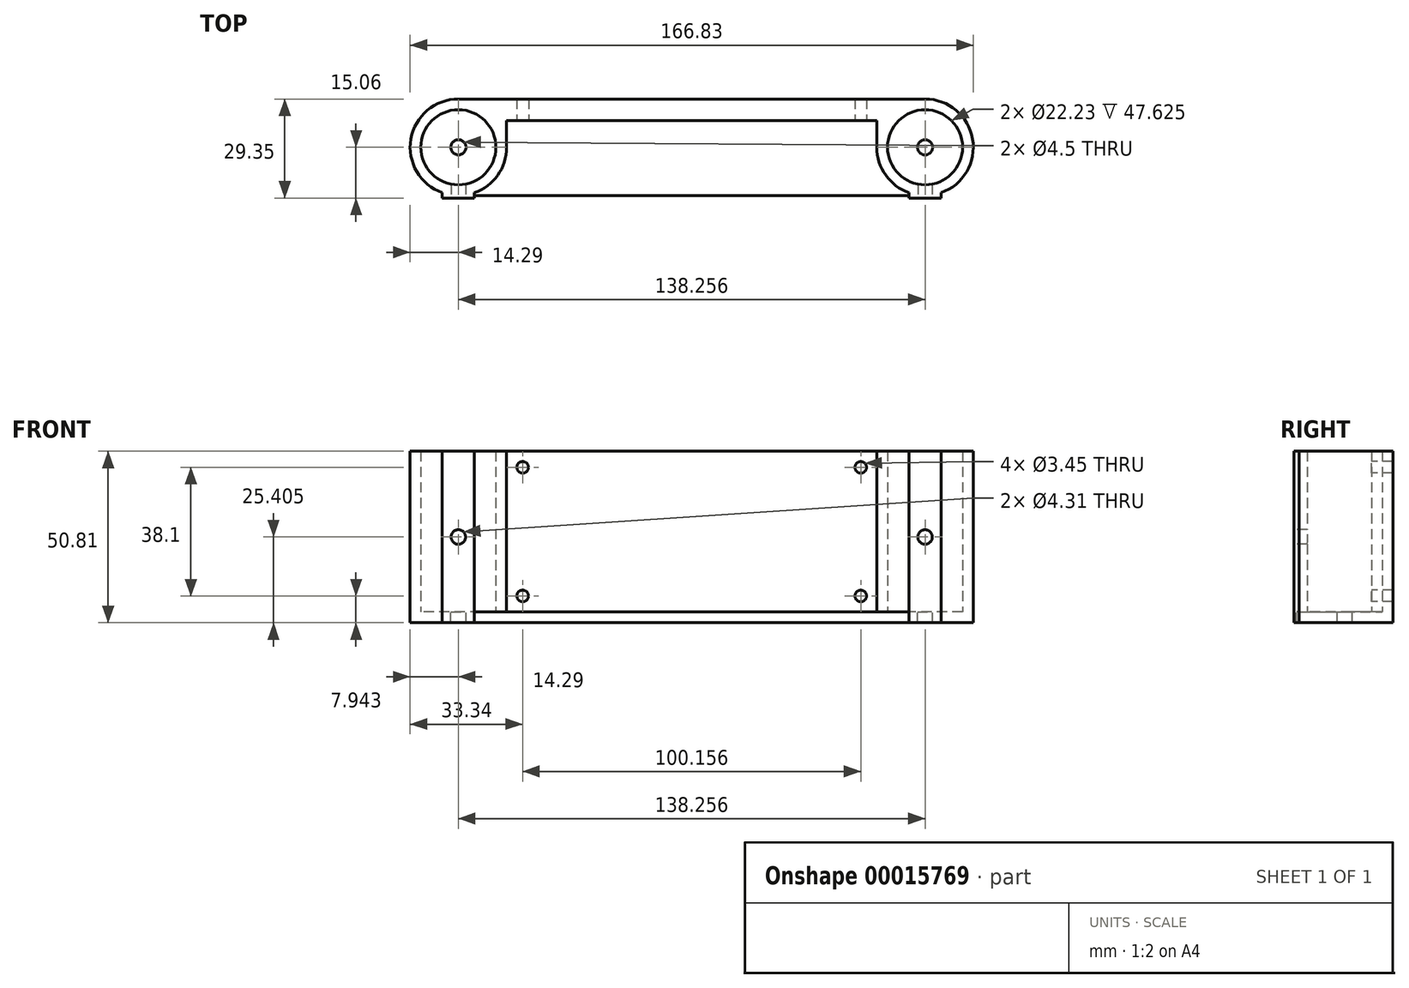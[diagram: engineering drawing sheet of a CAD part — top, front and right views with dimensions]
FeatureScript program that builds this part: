
annotation { "Feature Type Name" : "Feature", "Feature Type Description" : "" }
export const myFeature = defineFeature(function(context is Context, id is Id, definition is map)
    precondition{}
    {
        {
            var Q0;
            Q0=qCreatedBy(makeId("Top.planeOp"),FACE);
            var sketch = newSketch(context, id + "F0", { "sketchPlane" : qUnion([Q0])});
            skCircle(sketch, "E0", {"center": v(0, 0) * mm, "radius": 11.11 * mm});
            skLineSegment(sketch, "E1.bottom", {"start": v(14.29, 7.94) * mm, "end": v(123.97, 7.94) * mm});
            skLineSegment(sketch, "E2", {"start": v(69.13, 7.94) * mm, "end": v(69.13, 14.29) * mm, "construction": true});
            skCircle(sketch, "E3", {"center": v(138.26, 0) * mm, "radius": 11.11 * mm});
            skLineSegment(sketch, "E4", {"start": v(0, 14.29) * mm, "end": v(138.26, 14.29) * mm});
            skLineSegment(sketch, "E5", {"start": v(0, 0) * mm, "end": v(138.26, 0) * mm, "construction": true});
            skLineSegment(sketch, "E6", {"start": v(123.97, 7.94) * mm, "end": v(123.97, 0) * mm});
            skArc(sketch, "E7", {"start": v(0, 14.29) * mm, "mid": v(-14.08, 2.42) * mm, "end": v(-4.76, -13.47) * mm});
            skLineSegment(sketch, "E8", {"start": v(0, 0) * mm, "end": v(0, -13.47) * mm, "construction": true});
            skLineSegment(sketch, "E9", {"start": v(138.26, 0) * mm, "end": v(138.26, -13.47) * mm, "construction": true});
            skLineSegment(sketch, "E10.bottom", {"start": v(-4.76, -13.47) * mm, "end": v(4.76, -13.47) * mm, "construction": true});
            skLineSegment(sketch, "E10.top", {"start": v(-4.76, -15.06) * mm, "end": v(4.76, -15.06) * mm});
            skLineSegment(sketch, "E10.left", {"start": v(-4.76, -13.47) * mm, "end": v(-4.76, -15.06) * mm});
            skLineSegment(sketch, "E10.right", {"start": v(4.76, -13.47) * mm, "end": v(4.76, -15.06) * mm});
            skLineSegment(sketch, "E11.bottom", {"start": v(133.5, -13.47) * mm, "end": v(143.02, -13.47) * mm, "construction": true});
            skLineSegment(sketch, "E11.top", {"start": v(133.5, -15.06) * mm, "end": v(143.02, -15.06) * mm});
            skLineSegment(sketch, "E11.left", {"start": v(133.5, -13.47) * mm, "end": v(133.5, -15.06) * mm});
            skLineSegment(sketch, "E11.right", {"start": v(143.02, -13.47) * mm, "end": v(143.02, -15.06) * mm});
            skArc(sketch, "E12", {"start": v(123.97, 0) * mm, "mid": v(126.6, -8.25) * mm, "end": v(133.5, -13.47) * mm});
            skArc(sketch, "E13", {"start": v(143.02, -13.47) * mm, "mid": v(152.34, 2.42) * mm, "end": v(138.26, 14.29) * mm});
            skLineSegment(sketch, "E14", {"start": v(14.29, 7.94) * mm, "end": v(14.29, 0) * mm});
            skArc(sketch, "E15", {"start": v(4.76, -13.47) * mm, "mid": v(11.67, -8.25) * mm, "end": v(14.29, 0) * mm});
            skSolve(sketch);
        }
        {
            var Q0;
            Q0=qSketchRegion(id+"F0",true);
            extrude(context, id + "F1", {"entities" : qUnion([Q0]), "depth" : 47.62 * mm});
        }
        {
            var Q0;
            Q0=makeQuery(id+"F1.opExtrude","CAP_FACE",FACE,{"disambiguationData":[OSD([sQuery(id+"F0.wireOp",EDGE,"E0"),sQuery(id+"F0.wireOp",EDGE,"2iOkBpD2-QLiU-HpJU-IKXQ-EcRK06cCBt2a"),sQuery(id+"F0.wireOp",EDGE,"E1.bottom"),sQuery(id+"F0.wireOp",EDGE,"LR8YGM2p-kzYz-Rjs2-wGc3-v6aphVCy7C40"),sQuery(id+"F0.wireOp",EDGE,"E3"),sQuery(id+"F0.wireOp",EDGE,"E4"),sQuery(id+"F0.wireOp",EDGE,"a1pcXIPp-AWSM-aF7N-H1JB-dh9VYmGUxMzi"),sQuery(id+"F0.wireOp",EDGE,"5BYM6prM-a9B3-O1rF-SOB5-sMuNnPx88GNX"),sQuery(id+"F0.wireOp",EDGE,"E6"),sQuery(id+"F0.wireOp",EDGE,"teNxZqr3-d8HX-wysD-aT8M-tF9vT66hEsqo")])],"isStart":true});
            var sketch = newSketch(context, id + "F2", { "sketchPlane" : qUnion([Q0])});
            skLineSegment(sketch, "E16", {"start": v(0, 0) * mm, "end": v(0, 14.29) * mm, "construction": true});
            skLineSegment(sketch, "E17", {"start": v(138.26, 14.29) * mm, "end": v(138.26, 0) * mm, "construction": true});
            skLineSegment(sketch, "E18", {"start": v(138.26, 0) * mm, "end": v(0, 0) * mm, "construction": true});
            skLineSegment(sketch, "E19", {"start": v(138.26, 14.29) * mm, "end": v(0, 14.29) * mm});
            skCircle(sketch, "E20", {"center": v(0, 0) * mm, "radius": 2.25 * mm});
            skCircle(sketch, "E21", {"center": v(138.26, 0) * mm, "radius": 2.25 * mm});
            skSolve(sketch);
        }
        {
            var Q0;
            Q0=makeQuery(id+"F2.imprint","IMPRINT",FACE,{"disambiguationData":[TD([[makeQuery(id+"F2.imprint","IMPRINT",EDGE,{"derivedFrom":makeQuery(id+"F1.opExtrude","CAP_EDGE",EDGE,{"disambiguationData":[OSD([sQuery(id+"F0.wireOp",EDGE,"E0")])],"isStart":true})}),1.0]])]});
            var Q1;
            {var subQ2=sQuery(id+"F2.wireOp",EDGE,"SS8bNy7h-Ow7b-Kn8b-ZiMt-BjL3enOZ3Box");Q1=makeQuery(id+"F2.imprint","IMPRINT",FACE,{"disambiguationData":[TD([[makeQuery(id+"F2.imprint","IMPRINT",EDGE,{"derivedFrom":subQ2}),-1.0]])]});}
            var Q2;
            Q2=makeQuery(id+"F2.imprint","IMPRINT",FACE,{"disambiguationData":[TD([[makeQuery(id+"F2.imprint","IMPRINT",EDGE,{"derivedFrom":sQuery(id+"F2.wireOp",EDGE,"DZOvOBiB-ObCU-oQvi-dqaK-XYJ2mRQJM86I")}),-1.0]])]});
            var Q3;
            Q3=makeQuery(id+"F2.imprint","IMPRINT",FACE,{"disambiguationData":[TD([[makeQuery(id+"F2.imprint","IMPRINT",EDGE,{"derivedFrom":makeQuery(id+"F1.opExtrude","CAP_EDGE",EDGE,{"disambiguationData":[OSD([sQuery(id+"F0.wireOp",EDGE,"E1.bottom")])],"isStart":true})}),1.0]])]});
            var Q4;
            Q4=makeQuery(id+"F2.imprint","IMPRINT",FACE,{"disambiguationData":[TD([[makeQuery(id+"F2.imprint","IMPRINT",EDGE,{"derivedFrom":sQuery(id+"F2.wireOp",EDGE,"E20")}),-1.0]])]});
            var Q5;
            Q5=makeQuery(id+"F2.imprint","IMPRINT",FACE,{"disambiguationData":[TD([[makeQuery(id+"F2.imprint","IMPRINT",EDGE,{"derivedFrom":sQuery(id+"F2.wireOp",EDGE,"E21")}),-1.0]])]});
            extrude(context, id + "F3", {"entities" : qUnion([Q0, Q1, Q2, Q3, Q4, Q5]), "operationType" : NewBodyOperationType.ADD, "depth" : 3.17 * mm});
        }
        {
            var Q0;
            Q0=makeQuery(id+"F1.opExtrude","SWEPT_FACE",FACE,{"disambiguationData":[OSD([sQuery(id+"F0.wireOp",EDGE,"E1.bottom")])]});
            var sketch = newSketch(context, id + "F4", { "sketchPlane" : qUnion([Q0])});
            skLineSegment(sketch, "E22.bottom", {"start": v(14.29, 47.63) * mm, "end": v(19.05, 47.63) * mm, "construction": true});
            skLineSegment(sketch, "E22.top", {"start": v(14.29, 42.86) * mm, "end": v(19.05, 42.86) * mm, "construction": true});
            skLineSegment(sketch, "E22.left", {"start": v(14.29, 47.63) * mm, "end": v(14.29, 42.86) * mm, "construction": true});
            skLineSegment(sketch, "E22.right", {"start": v(19.05, 47.63) * mm, "end": v(19.05, 42.86) * mm, "construction": true});
            skLineSegment(sketch, "E23", {"start": v(69.13, 47.63) * mm, "end": v(69.13, 0) * mm, "construction": true});
            skLineSegment(sketch, "E24.bottom", {"start": v(19.05, 42.86) * mm, "end": v(119.2, 42.86) * mm, "construction": true});
            skLineSegment(sketch, "E24.top", {"start": v(19.05, 4.76) * mm, "end": v(119.2, 4.76) * mm, "construction": true});
            skLineSegment(sketch, "E24.left", {"start": v(19.05, 42.86) * mm, "end": v(19.05, 4.76) * mm, "construction": true});
            skLineSegment(sketch, "E24.right", {"start": v(119.2, 42.86) * mm, "end": v(119.2, 4.76) * mm, "construction": true});
            skPoint(sketch, "E24.middle", {"position": v(69.13, 23.81) * mm});
            skCircle(sketch, "E25", {"center": v(19.05, 42.86) * mm, "radius": 1.73 * mm});
            skCircle(sketch, "E26", {"center": v(19.05, 4.76) * mm, "radius": 1.73 * mm});
            skCircle(sketch, "E27", {"center": v(119.2, 4.76) * mm, "radius": 1.73 * mm});
            skCircle(sketch, "E28", {"center": v(119.2, 42.86) * mm, "radius": 1.73 * mm});
            skSolve(sketch);
        }
        {
            var Q0;
            Q0=qSketchRegion(id+"F4",true);
            var Q1;
            {var subQ0=sQuery(id+"F0.wireOp",EDGE,"E4");Q1=makeQuery(id+"F3.boolean.opBoolean","MERGE",FACE,{"derivedFrom":[makeQuery(id+"F1.opExtrude","SWEPT_FACE",FACE,{"disambiguationData":[OSD([subQ0])]}),makeQuery(id+"F3.opExtrude","SWEPT_FACE",FACE,{"disambiguationData":[OSD([subQ0])]})]});}
            extrude(context, id + "F5", {"entities" : qUnion([Q0]), "operationType" : NewBodyOperationType.REMOVE, "endBound" : BoundingType.UP_TO_SURFACE, "oppositeDirection" : true, "endBoundEntityFace" : qUnion([Q1]), "depth" : 25.4 * mm});
        }
        {
            var Q0;
            {var subQ0=sQuery(id+"F0.wireOp",EDGE,"E11.top");Q0=makeQuery(id+"F3.boolean.opBoolean","MERGE",FACE,{"derivedFrom":[makeQuery(id+"F1.opExtrude","SWEPT_FACE",FACE,{"disambiguationData":[OSD([sQuery(id+"F0.wireOp",EDGE,"E10.top")])]}),makeQuery(id+"F1.opExtrude","SWEPT_FACE",FACE,{"disambiguationData":[OSD([subQ0])]}),makeQuery(id+"F3.opExtrude","SWEPT_FACE",FACE,{"disambiguationData":[OSD([subQ0,sQuery(id+"F2.wireOp",EDGE,"SS8bNy7h-Ow7b-Kn8b-ZiMt-BjL3enOZ3Box")])]})]});}
            var sketch = newSketch(context, id + "F6", { "sketchPlane" : qUnion([Q0])});
            skLineSegment(sketch, "E29", {"start": v(0, 47.63) * mm, "end": v(0, -3.17) * mm, "construction": true});
            skLineSegment(sketch, "E30", {"start": v(138.26, 47.63) * mm, "end": v(138.26, -3.18) * mm, "construction": true});
            skCircle(sketch, "E31", {"center": v(0, 22.23) * mm, "radius": 2.15 * mm});
            skCircle(sketch, "E32", {"center": v(138.26, 22.23) * mm, "radius": 2.15 * mm});
            skSolve(sketch);
        }
        {
            var Q0;
            Q0=qSketchRegion(id+"F6",true);
            var Q1;
            {var subQ0=sQuery(id+"F0.wireOp",EDGE,"E0");Q1=makeQuery(id+"F3.boolean.opBoolean","MERGE",FACE,{"derivedFrom":[makeQuery(id+"F1.opExtrude","SWEPT_FACE",FACE,{"disambiguationData":[OSD([subQ0])]}),makeQuery(id+"F3.opExtrude","SWEPT_FACE",FACE,{"disambiguationData":[OSD([subQ0])]})]});}
            extrude(context, id + "F7", {"entities" : qUnion([Q0]), "operationType" : NewBodyOperationType.REMOVE, "oppositeDirection" : true, "endBoundEntityFace" : qUnion([Q1]), "depth" : 6.35 * mm});
        }
    });
